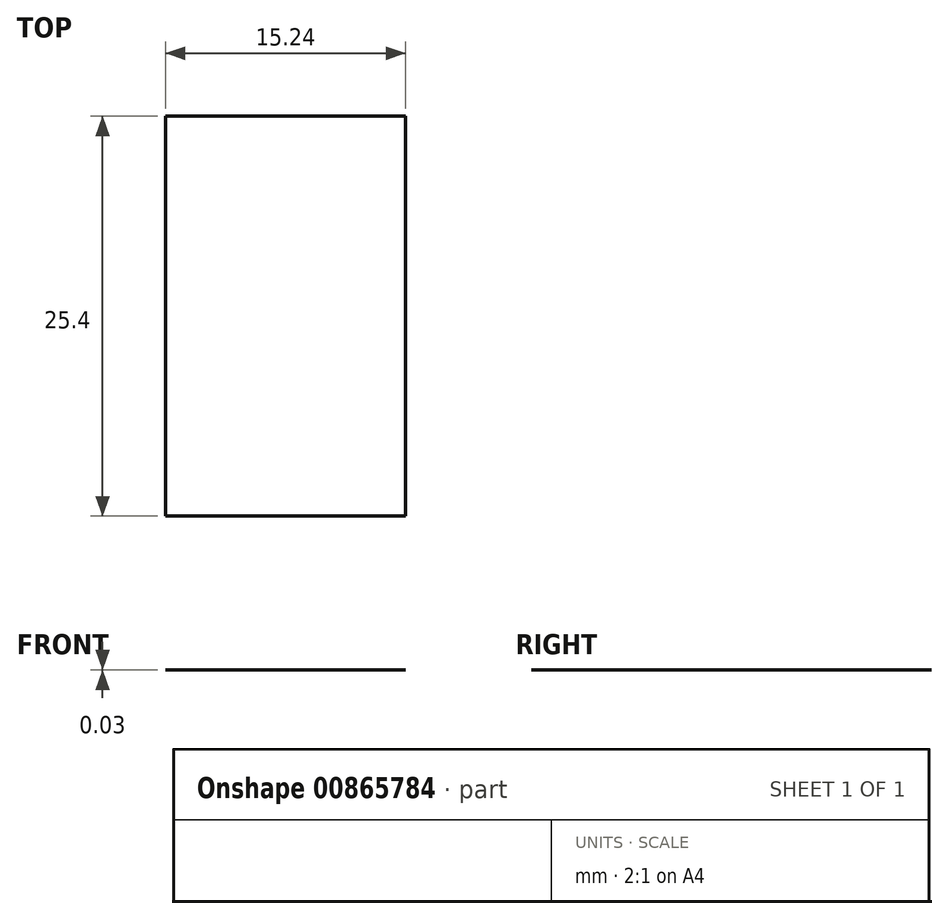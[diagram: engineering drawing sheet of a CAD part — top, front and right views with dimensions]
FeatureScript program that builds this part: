
annotation { "Feature Type Name" : "Feature", "Feature Type Description" : "" }
export const myFeature = defineFeature(function(context is Context, id is Id, definition is map)
    precondition{}
    {
        {
            var Q0;
            Q0=qCreatedBy(makeId("Top.planeOp"),FACE);
            var sketch = newSketch(context, id + "F0", { "sketchPlane" : qUnion([Q0])});
            skLineSegment(sketch, "E0.bottom", {"start": v(0, 0) * mm, "end": v(15.24, 0) * mm});
            skLineSegment(sketch, "E0.top", {"start": v(0, 25.4) * mm, "end": v(15.24, 25.4) * mm});
            skLineSegment(sketch, "E0.left", {"start": v(0, 0) * mm, "end": v(0, 25.4) * mm});
            skLineSegment(sketch, "E0.right", {"start": v(15.24, 0) * mm, "end": v(15.24, 25.4) * mm});
            skSolve(sketch);
        }
        {
            var Q0;
            Q0 = qSketchRegion(id + "F0", true);
            extrude(context, id + "F1", {"entities" : qUnion([Q0]), "depth" : 0.03 * mm, "offsetDistance" : 25.4 * mm});
        }
    });
